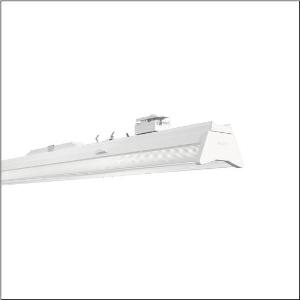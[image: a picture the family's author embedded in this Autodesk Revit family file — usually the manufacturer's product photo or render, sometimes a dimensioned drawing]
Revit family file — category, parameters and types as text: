
# Revit family: licross_r__21_performance_mo_52td16cn46xg_4d89
name_source: partatom
category: Lighting Fixtures
units: mm (PartAtom-declared; Revit-internal decimal feet)

## family parameters
Cut with Voids When Loaded = No
Host = Face
Light Source = No
Part Type = Normal
Room Calculation Point = No
Round Connector Dimension = Use Diameter
Shared = No

## types (1)
- --- (1 x LED, 6000 lm, 32 W, 4000K)
    Apparent Load = 32 VA
    CIE Flux Codes = 66 88 96 79 100
    Color Rendering = 80
    Color Temperature = 4000K
    Default Elevation = 1800 mm
    Description = Licross® 21 Performance MO, luminaire insert, of sheet steel, galvanised, coil coated, white, length: 1.500mm, width: 120mm, height: 123mm, LED rated luminous flux: 6.000lm, light colour: 840, control gear: ON/OFF Multilumen, CLOi, control gear: ECG Multilumen, with plug, 3-pole, with phase selection, mains connection: 220..240V, AC, 50/60Hz, start of lifetime: 32W, end of service life: 38W, halogen-free wiring, primary light control with lens, of plastic, primary optical cover: cover, of PMMA, light emission: direct/indirect distribution, primary light characteristic: symmetric, protection rating (complete): IP54, insulation class (complete): insulation class I (protective earthing), certification: CE, ENEC, UKCA, protection symbol: D if used in an environment with non-conductive dust loads with corresponding accessories, impact resistance: IK06, permissible ambient temperature for indoor applications: -35..+55°C, corresponds to IFS (International Featured Standards) requirements for safety and quality in the food industry, reducing of maximum allowable ambient temperature of 5°C with ceiling mounting, LABS conformity tested according to VDMA 24364:2018-05, packaging unit: 1 piece
    Height = 114 mm
    Lamp = 1 x LED
    Lamp Light Flux = 6000 lm
    Lamp Power = 32 W
    Lamp count = 1
    Length = 1500 mm
    Luminous efficacy = 188 lm/W
    Manufacturer = Siteco
    ModVariant = No
    Model = 52TD16CN46XG
    Mounting Place = Ceiling
    Mounting Type = Pendant
    Number of Poles = 1
    OnlyDefault = Yes
    Power Factor = 1
    Product Name = Licross® 21 Performance MO
    Product group = luminaire insert
    ProductGroupID = 901
    Protection Class = Protection class I
    Protection Degree = IP 54
    RLX_Detail_Level = 1
    RLX_Emergency_Light_Flux = 0 lm
    RLX_Emergency_Type = 0
    RLX_Emergency_Type_DB = No
    RlxData = <blob elided: 31869 chars, md5=1969c078>
    Socket = socket
    Standby Power = 0 W
    System Light Flux = 6000 lm
    System Power = 32 W
    Type Comments = factory setting: luminous flux: 100 % | (A | C | E) | 74 mA
    Type Image = l_1256138.jpg
    URL = http://relux.com
    VarID = @adj_059791
    Voltage = 0 V
    Weight = 0.00 kg
    Width = 120 mm

## geometry (parser evidence)
native form markers: Blend x4, Sweep x11
no freeform markers — native parametric forms only
